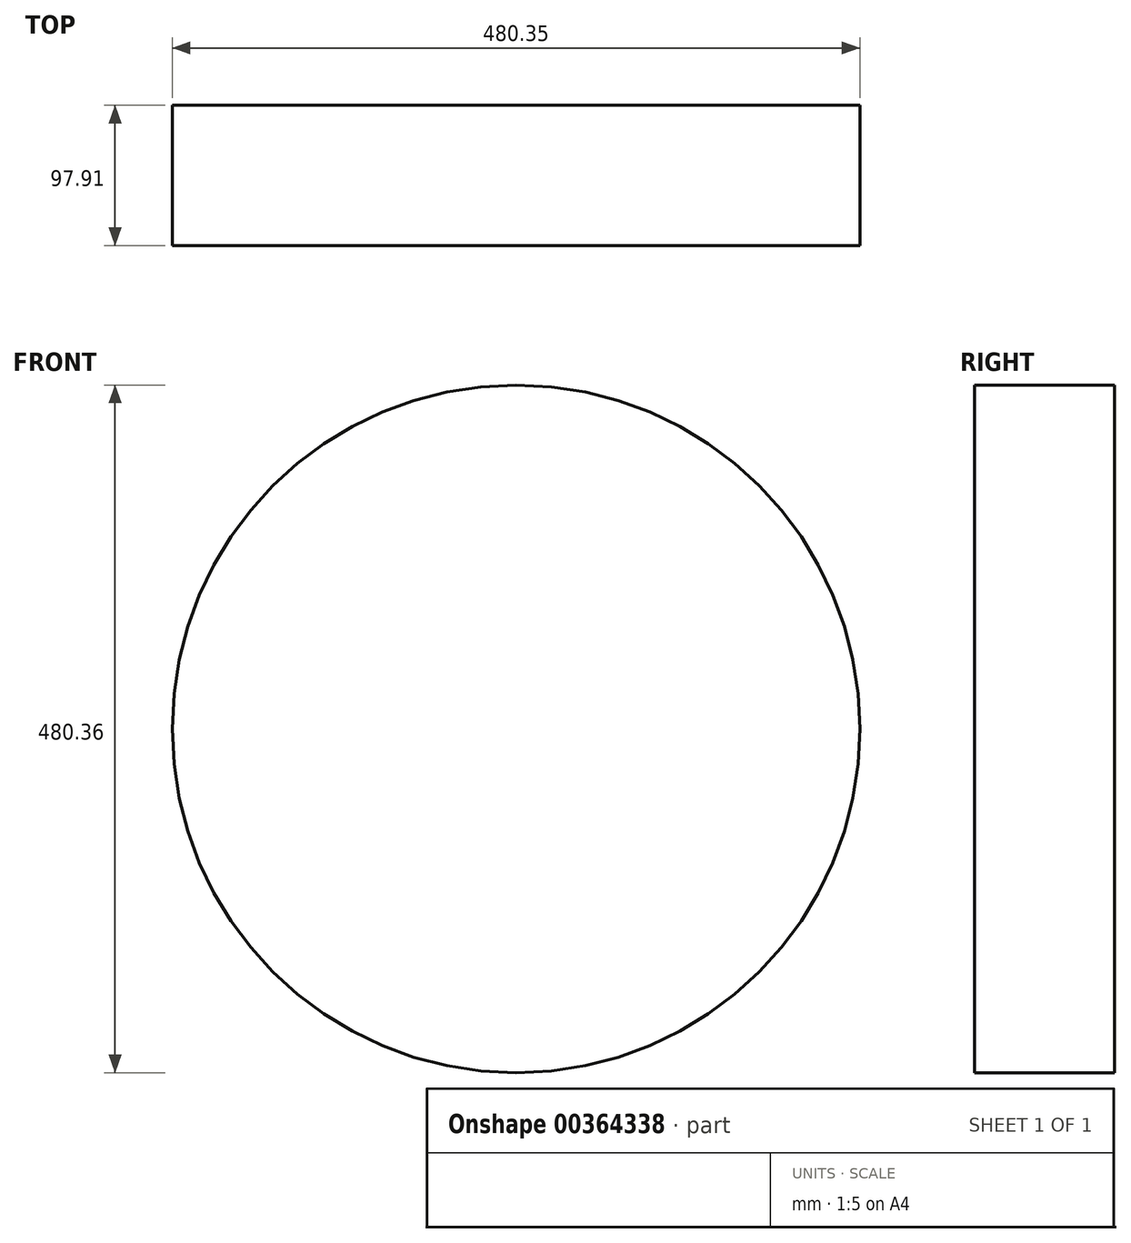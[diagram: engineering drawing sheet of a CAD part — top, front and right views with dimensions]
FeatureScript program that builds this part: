
annotation { "Feature Type Name" : "Feature", "Feature Type Description" : "" }
export const myFeature = defineFeature(function(context is Context, id is Id, definition is map)
    precondition{}
    {
        {
            var Q0;
            Q0=qCreatedBy(makeId("Front.planeOp"),FACE);
            var sketch = newSketch(context, id + "F0", { "sketchPlane" : qUnion([Q0])});
            skCircle(sketch, "E0", {"center": v(-27.9, 0) * mm, "radius": 240.18 * mm});
            skSolve(sketch);
        }
        {
            var Q0;
            Q0 = qSketchRegion(id + "F0", true);
            extrude(context, id + "F1", {"entities" : qUnion([Q0]), "depth" : 97.9 * mm});
        }
    });
